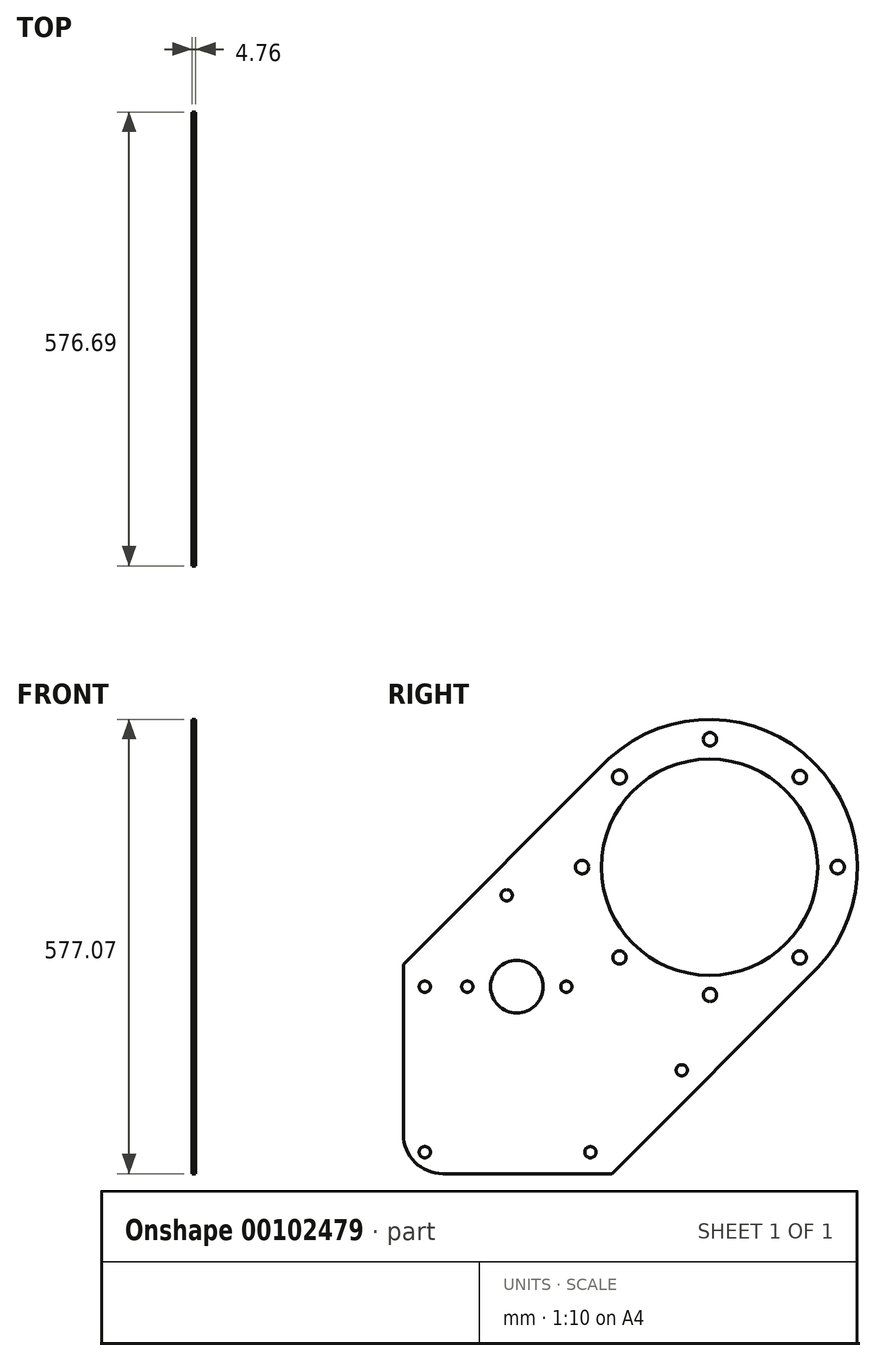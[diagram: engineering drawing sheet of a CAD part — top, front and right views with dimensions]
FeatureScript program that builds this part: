
annotation { "Feature Type Name" : "Feature", "Feature Type Description" : "" }
export const myFeature = defineFeature(function(context is Context, id is Id, definition is map)
    precondition{}
    {
        {
            var Q0;
            Q0=qCreatedBy(makeId("Right.planeOp"),FACE);
            var sketch = newSketch(context, id + "F0", { "sketchPlane" : qUnion([Q0])});
            skArc(sketch, "E0", {"start": v(-271.7, -221.9) * mm, "mid": v(-257.05, -257.25) * mm, "end": v(-221.7, -271.9) * mm});
            skArc(sketch, "E1", {"start": v(254.99, -10.18) * mm, "mid": v(250.02, 250.15) * mm, "end": v(-10.3, 255.25) * mm});
            skLineSegment(sketch, "E2", {"start": v(-221.7, -271.9) * mm, "end": v(-6.54, -271.9) * mm});
            skLineSegment(sketch, "E3", {"start": v(-271.7, -221.9) * mm, "end": v(-271.7, -5.95) * mm});
            skCircle(sketch, "E4", {"center": v(117.21, 117.4) * mm, "radius": 137.32 * mm});
            skCircle(sketch, "E5", {"center": v(-127.66, -34.4) * mm, "radius": 33.34 * mm});
            skCircle(sketch, "E6", {"center": v(-190.57, -34.4) * mm, "radius": 7.14 * mm});
            skCircle(sketch, "E7", {"center": v(-64.75, -34.4) * mm, "radius": 7.14 * mm});
            skCircle(sketch, "E8", {"center": v(81.85, -140.54) * mm, "radius": 7.14 * mm});
            skCircle(sketch, "E9", {"center": v(-140.56, 81.73) * mm, "radius": 7.14 * mm});
            skCircle(sketch, "E10", {"center": v(-244.52, -34.4) * mm, "radius": 7.14 * mm});
            skCircle(sketch, "E11", {"center": v(-34.2, -244.57) * mm, "radius": 7.14 * mm});
            skCircle(sketch, "E12", {"center": v(-244.52, -244.57) * mm, "radius": 7.14 * mm});
            skCircle(sketch, "E13", {"center": v(2.66, 231.96) * mm, "radius": 8.9 * mm});
            skCircle(sketch, "E14", {"center": v(117.6, 279.9) * mm, "radius": 8.5 * mm});
            skCircle(sketch, "E15", {"center": v(231.8, 232) * mm, "radius": 8.5 * mm});
            skCircle(sketch, "E16", {"center": v(-44.8, 117.58) * mm, "radius": 8.5 * mm});
            skCircle(sketch, "E17", {"center": v(279.94, 117.58) * mm, "radius": 8.5 * mm});
            skCircle(sketch, "E18", {"center": v(2.73, 2.77) * mm, "radius": 8.5 * mm});
            skCircle(sketch, "E19", {"center": v(117.69, -44.9) * mm, "radius": 8.5 * mm});
            skCircle(sketch, "E20", {"center": v(231.7, 2.79) * mm, "radius": 8.5 * mm});
            skLineSegment(sketch, "E21", {"start": v(-6.54, -271.9) * mm, "end": v(254.99, -10.18) * mm});
            skLineSegment(sketch, "E22", {"start": v(-271.7, -5.95) * mm, "end": v(-10.3, 255.25) * mm});
            skSolve(sketch);
        }
        {
            var Q0;
            Q0 = qSketchRegion(id + "F0", true);
            extrude(context, id + "F1", {"entities" : qUnion([Q0]), "depth" : 4.76 * mm});
        }
    });
